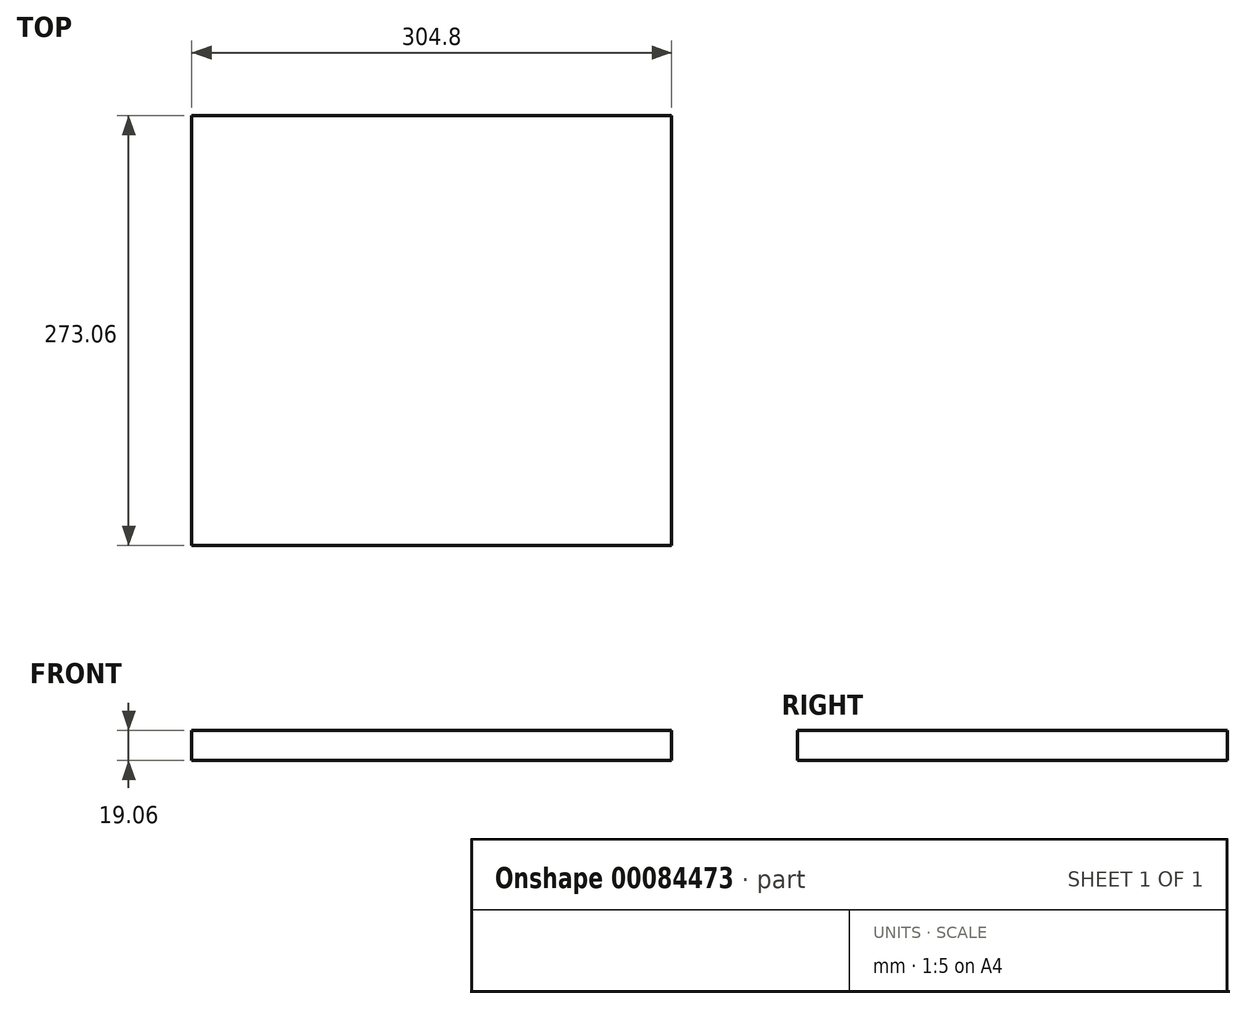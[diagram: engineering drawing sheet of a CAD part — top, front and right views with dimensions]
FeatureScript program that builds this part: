
annotation { "Feature Type Name" : "Feature", "Feature Type Description" : "" }
export const myFeature = defineFeature(function(context is Context, id is Id, definition is map)
    precondition{}
    {
        {
            var Q0;
            Q0=qCreatedBy(makeId("Front.planeOp"),FACE);
            var sketch = newSketch(context, id + "F0", { "sketchPlane" : qUnion([Q0])});
            skLineSegment(sketch, "E0.bottom", {"start": v(152.4, -9.52) * mm, "end": v(-152.4, -9.53) * mm});
            skLineSegment(sketch, "E0.top", {"start": v(152.4, 9.53) * mm, "end": v(-152.4, 9.52) * mm});
            skLineSegment(sketch, "E0.left", {"start": v(152.4, -9.52) * mm, "end": v(152.4, 9.53) * mm});
            skLineSegment(sketch, "E0.right", {"start": v(-152.4, -9.53) * mm, "end": v(-152.4, 9.52) * mm});
            skPoint(sketch, "E0.middle", {"position": v(0, 0) * mm});
            skSolve(sketch);
        }
        {
            var Q0;
            Q0 = qSketchRegion(id + "F0", true);
            extrude(context, id + "F1", {"entities" : qUnion([Q0]), "endBound" : BoundingType.SYMMETRIC, "depth" : 273.05 * mm});
        }
    });
